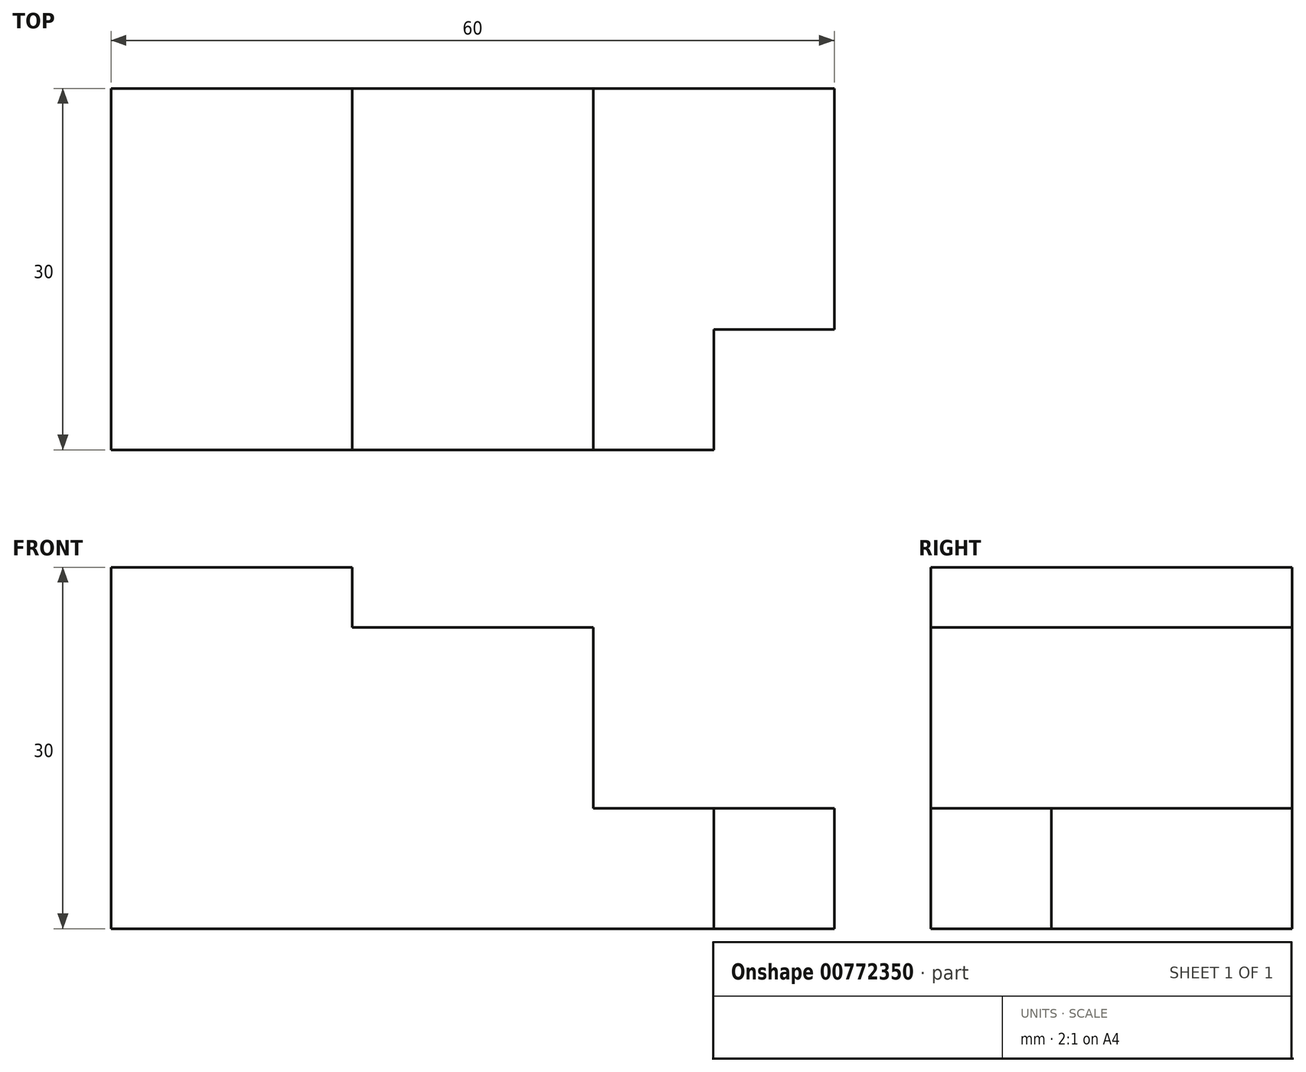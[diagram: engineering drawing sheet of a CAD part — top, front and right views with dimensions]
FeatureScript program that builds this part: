
annotation { "Feature Type Name" : "Feature", "Feature Type Description" : "" }
export const myFeature = defineFeature(function(context is Context, id is Id, definition is map)
    precondition{}
    {
        {
            var Q0;
            Q0=qCreatedBy(makeId("Front.planeOp"),FACE);
            var sketch = newSketch(context, id + "F0", { "sketchPlane" : qUnion([Q0])});
            skLineSegment(sketch, "E0", {"start": v(0, 0) * mm, "end": v(60, 0) * mm});
            skLineSegment(sketch, "E1", {"start": v(60, 0) * mm, "end": v(60, 10) * mm});
            skLineSegment(sketch, "E2", {"start": v(60, 10) * mm, "end": v(40, 10) * mm});
            skLineSegment(sketch, "E3", {"start": v(40, 10) * mm, "end": v(40, 25) * mm});
            skLineSegment(sketch, "E4", {"start": v(40, 25) * mm, "end": v(20, 25) * mm});
            skLineSegment(sketch, "E5", {"start": v(20, 25) * mm, "end": v(20, 30) * mm});
            skLineSegment(sketch, "E6", {"start": v(20, 30) * mm, "end": v(0, 30) * mm});
            skLineSegment(sketch, "E7", {"start": v(0, 30) * mm, "end": v(0, 0) * mm});
            skLineSegment(sketch, "E8", {"start": v(50, 10) * mm, "end": v(50, 0) * mm});
            skSolve(sketch);
        }
        {
            var Q0;
            Q0 = qSketchRegion(id + "F0", true);
            extrude(context, id + "F1", {"entities" : qUnion([Q0]), "oppositeDirection" : true, "depth" : 30 * mm, "offsetDistance" : 25 * mm});
        }
        {
            var Q0;
            {var subQ0=sQuery(id+"F0.wireOp",EDGE,"E1");Q0=makeQuery(id+"F0.imprint","IMPRINT",FACE,{"disambiguationData":[TD([[makeQuery(id+"F0.imprint","IMPRINT",EDGE,{"derivedFrom":subQ0}),1.0]])]});}
            extrude(context, id + "F2", {"entities" : qUnion([Q0]), "operationType" : NewBodyOperationType.REMOVE, "oppositeDirection" : true, "depth" : 10 * mm, "offsetDistance" : 25 * mm});
        }
    });
